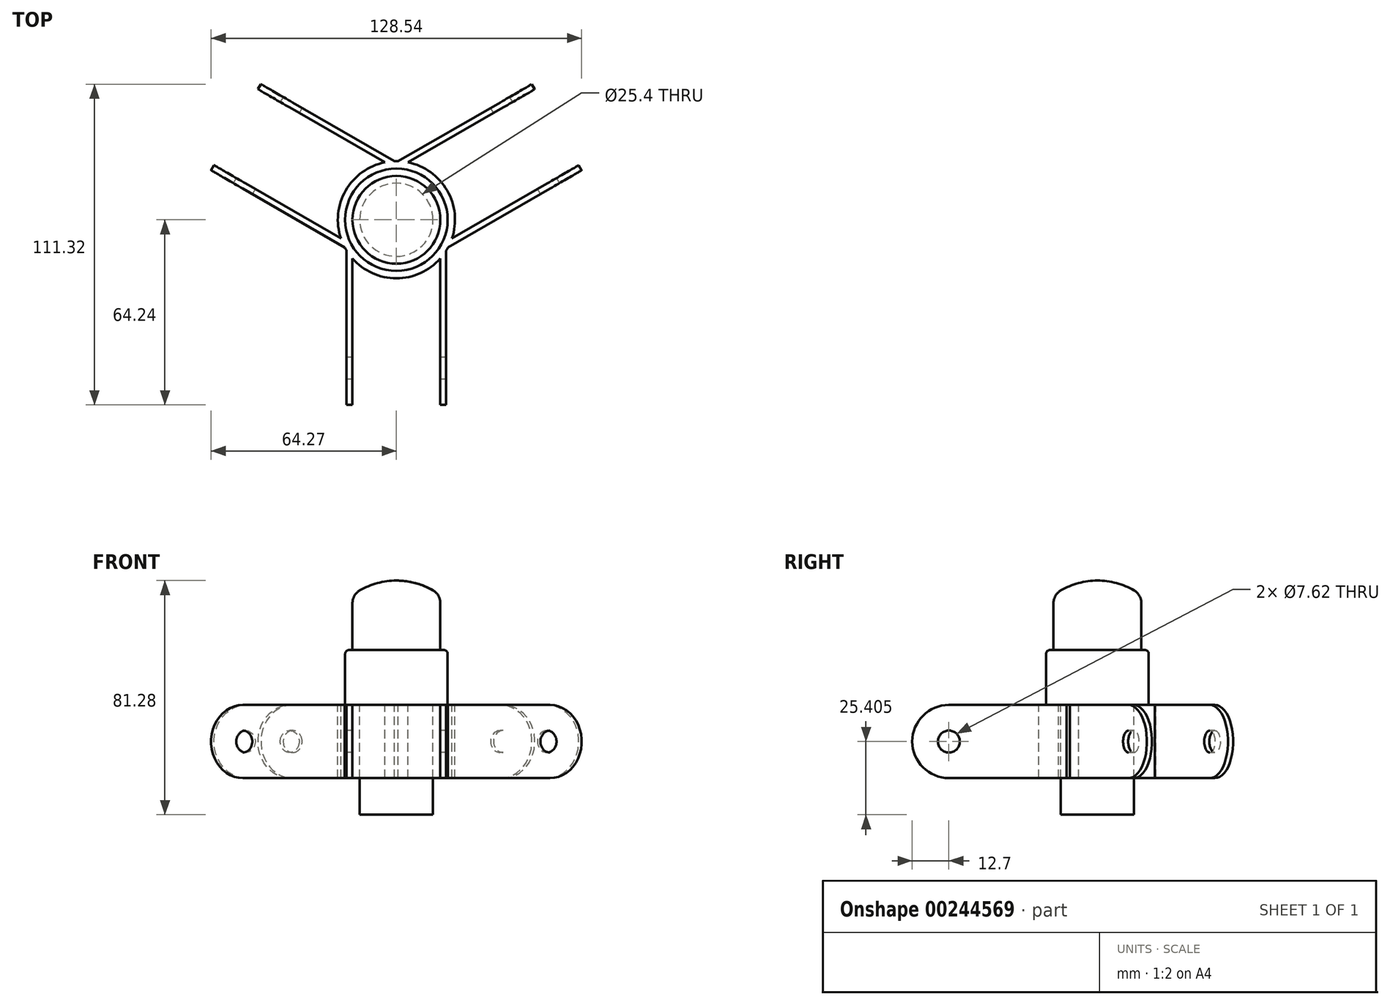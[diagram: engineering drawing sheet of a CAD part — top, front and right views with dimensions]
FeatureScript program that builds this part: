
annotation { "Feature Type Name" : "Feature", "Feature Type Description" : "" }
export const myFeature = defineFeature(function(context is Context, id is Id, definition is map)
    precondition{}
    {
        {
            var Q0;
            Q0=qCreatedBy(makeId("Front.planeOp"),FACE);
            var sketch = newSketch(context, id + "F0", { "sketchPlane" : qUnion([Q0])});
            skLineSegment(sketch, "E0.rect.top", {"start": v(15.24, -9.52) * mm, "end": v(0, -9.52) * mm});
            skLineSegment(sketch, "E0.rect.left", {"start": v(15.24, 9.53) * mm, "end": v(15.24, -9.52) * mm});
            skPoint(sketch, "E0.rect.middle", {"position": v(0, 0) * mm});
            skLineSegment(sketch, "E1", {"start": v(0, 65.3) * mm, "end": v(0, -40.02) * mm, "construction": true});
            skArc(sketch, "E2.0.MirrorCS", {"start": v(0, 14.6) * mm, "mid": v(8.03, 13.3) * mm, "end": v(15.24, 9.53) * mm});
            skLineSegment(sketch, "E3", {"start": v(0, 14.6) * mm, "end": v(0, -9.52) * mm});
            skPoint(sketch, "E4.center.orphan", {"position": v(0, -12.6) * mm});
            skPoint(sketch, "E0.rect.right.start.orphan", {"position": v(-15.24, 9.53) * mm});
            skPoint(sketch, "E5.orphan", {"position": v(-15.24, -9.52) * mm});
            skSolve(sketch);
        }
        {
            var Q0;
            Q0=makeQuery(id+"F0.imprint","IMPRINT",FACE,{"disambiguationData":[TD([[makeQuery(id+"F0.imprint","IMPRINT",EDGE,{"derivedFrom":sQuery(id+"F0.wireOp",EDGE,"E0.rect.top")}),-1.0]])]});
            var Q1;
            Q1=sQuery(id+"F0.wireOp",EDGE,"E1");
            revolve(context, id + "F1", {"entities" : qUnion([Q0]), "axis" : qUnion([Q1]), "revolveType" : RevolveType.FULL});
        }
        {
            var Q0;
            Q0=makeQuery(id+"F1.opRevolve","SWEPT_EDGE",EDGE,{"disambiguationData":[OSD([sQuery(id+"F0.wireOp",EDGE,"E0.rect.left"),sQuery(id+"F0.wireOp",EDGE,"E2.0.MirrorCS")])]});
            fillet(context, id + "F2", {"entities" : qUnion([Q0]), "radius" : 5.08 * mm, "tangentPropagation" : true, "allowEdgeOverflow" : false});
        }
        {
            var Q0;
            Q0=makeQuery(id+"F1.opRevolve","SWEPT_FACE",FACE,{"disambiguationData":[OSD([sQuery(id+"F0.wireOp",EDGE,"E0.rect.top")])]});
            var sketch = newSketch(context, id + "F3", { "sketchPlane" : qUnion([Q0])});
            skCircle(sketch, "E6", {"center": v(0, 0) * mm, "radius": 17.78 * mm});
            skSolve(sketch);
        }
        {
            var Q0;
            Q0=makeQuery(id+"F3.imprint","IMPRINT",FACE,{"disambiguationData":[TD([[makeQuery(id+"F3.imprint","IMPRINT",EDGE,{"derivedFrom":sQuery(id+"F3.wireOp",EDGE,"E6")}),1.0]])]});
            var Q1;
            Q1=makeQuery(id+"F3.imprint","IMPRINT",FACE,{"disambiguationData":[TD([[makeQuery(id+"F3.imprint","IMPRINT",EDGE,{"derivedFrom":makeQuery(id+"F1.opRevolve","SWEPT_EDGE",EDGE,{"disambiguationData":[OSD([sQuery(id+"F0.wireOp",EDGE,"E0.rect.top"),sQuery(id+"F0.wireOp",EDGE,"E0.rect.left")])]})}),-1.0]])]});
            extrude(context, id + "F4", {"entities" : qUnion([Q0, Q1]), "operationType" : NewBodyOperationType.ADD, "depth" : 19.05 * mm});
        }
        {
            var Q0;
            Q0=makeQuery(id+"F4.opExtrude","CAP_FACE",FACE,{"disambiguationData":[OSD([sQuery(id+"F3.wireOp",EDGE,"E6")])],"isStart":false});
            var sketch = newSketch(context, id + "F5", { "sketchPlane" : qUnion([Q0])});
            skCircle(sketch, "E7.0", {"center": v(0, 0) * mm, "radius": 12.7 * mm});
            skCircle(sketch, "E8.0", {"center": v(0, 0) * mm, "radius": 15.24 * mm});
            skSolve(sketch);
        }
        {
            var Q0;
            Q0=makeQuery(id+"F5.imprint","IMPRINT",FACE,{"disambiguationData":[TD([[makeQuery(id+"F5.imprint","IMPRINT",EDGE,{"derivedFrom":sQuery(id+"F5.wireOp",EDGE,"E7.0")}),1.0]])]});
            extrude(context, id + "F6", {"entities" : qUnion([Q0]), "operationType" : NewBodyOperationType.ADD, "depth" : 38.1 * mm});
        }
        {
            var Q0;
            {var subQ0=sQuery(id+"F3.wireOp",EDGE,"E6");Q0=makeQuery(id+"F6.boolean.opBoolean","SPLIT",FACE,{"disambiguationData":[TD([makeQuery(id+"F4.opExtrude","SWEPT_FACE",FACE,{"disambiguationData":[OSD([subQ0])]})])],"derivedFrom":makeQuery(id+"F4.opExtrude","CAP_FACE",FACE,{"disambiguationData":[OSD([subQ0])],"isStart":false})});}
            var sketch = newSketch(context, id + "F7", { "sketchPlane" : qUnion([Q0])});
            skArc(sketch, "E9", {"start": v(15.24, 13.44) * mm, "mid": v(0, 20.32) * mm, "end": v(-15.24, 13.44) * mm});
            skLineSegment(sketch, "E10", {"start": v(-15.24, 13.44) * mm, "end": v(-15.24, 64.24) * mm});
            skLineSegment(sketch, "E11", {"start": v(15.24, 13.44) * mm, "end": v(15.24, 64.24) * mm});
            skLineSegment(sketch, "E12", {"start": v(15.24, 64.24) * mm, "end": v(-15.24, 64.24) * mm, "construction": true});
            skLineSegment(sketch, "E13", {"start": v(-17.27, 64.24) * mm, "end": v(-17.27, 10.7) * mm});
            skLineSegment(sketch, "E14", {"start": v(-17.27, 10.7) * mm, "end": v(17.27, 10.7) * mm, "construction": true});
            skLineSegment(sketch, "E15", {"start": v(17.27, 10.7) * mm, "end": v(17.27, 64.24) * mm});
            skLineSegment(sketch, "E16", {"start": v(17.27, 64.24) * mm, "end": v(15.24, 64.24) * mm});
            skLineSegment(sketch, "E17", {"start": v(-17.27, 64.24) * mm, "end": v(-15.24, 64.24) * mm});
            skArc(sketch, "E18.trimOffspring", {"start": v(-17.27, 10.7) * mm, "mid": v(-17.6, 10.16) * mm, "end": v(-17.9, 9.6) * mm});
            skLineSegment(sketch, "E19.1.0", {"start": v(-19.26, 6.48) * mm, "end": v(-63.25, -18.92) * mm});
            skLineSegment(sketch, "E19.1.1", {"start": v(-4.02, -19.92) * mm, "end": v(-48.01, -45.32) * mm});
            skLineSegment(sketch, "E19.1.2", {"start": v(-47, -47.08) * mm, "end": v(-0.63, -20.31) * mm});
            skLineSegment(sketch, "E19.1.3", {"start": v(-64.27, -17.16) * mm, "end": v(-63.25, -18.92) * mm});
            skLineSegment(sketch, "E19.1.4", {"start": v(-17.9, 9.6) * mm, "end": v(-64.27, -17.16) * mm});
            skLineSegment(sketch, "E19.1.5", {"start": v(-47, -47.08) * mm, "end": v(-48.01, -45.32) * mm});
            skLineSegment(sketch, "E19.2.0", {"start": v(4.02, -19.92) * mm, "end": v(48.01, -45.32) * mm});
            skLineSegment(sketch, "E19.2.1", {"start": v(19.26, 6.48) * mm, "end": v(63.25, -18.92) * mm});
            skLineSegment(sketch, "E19.2.2", {"start": v(64.27, -17.16) * mm, "end": v(17.9, 9.6) * mm});
            skLineSegment(sketch, "E19.2.3", {"start": v(47, -47.08) * mm, "end": v(48.01, -45.32) * mm});
            skLineSegment(sketch, "E19.2.4", {"start": v(0.63, -20.31) * mm, "end": v(47, -47.08) * mm});
            skLineSegment(sketch, "E19.2.5", {"start": v(64.27, -17.16) * mm, "end": v(63.25, -18.92) * mm});
            skArc(sketch, "E20.trimOffspring", {"start": v(17.9, 9.6) * mm, "mid": v(17.6, 10.16) * mm, "end": v(17.27, 10.7) * mm});
            skArc(sketch, "E21.trimOffspring", {"start": v(4.02, -19.92) * mm, "mid": v(17.6, -10.16) * mm, "end": v(19.26, 6.48) * mm});
            skArc(sketch, "E22.trimOffspring", {"start": v(-0.63, -20.31) * mm, "mid": v(0, -20.32) * mm, "end": v(0.63, -20.31) * mm});
            skArc(sketch, "E23.trimOffspring", {"start": v(-19.26, 6.48) * mm, "mid": v(-17.6, -10.16) * mm, "end": v(-4.02, -19.92) * mm});
            skSolve(sketch);
        }
        {
            var Q0;
            Q0=makeQuery(id+"F7.imprint","IMPRINT",FACE,{"disambiguationData":[TD([[makeQuery(id+"F7.imprint","IMPRINT",EDGE,{"derivedFrom":sQuery(id+"F7.wireOp",EDGE,"E9")}),1.0]])]});
            var Q1;
            Q1=makeQuery(id+"F7.imprint","IMPRINT",FACE,{"disambiguationData":[TD([[makeQuery(id+"F7.imprint","IMPRINT",EDGE,{"derivedFrom":makeQuery(id+"F4.opExtrude","CAP_EDGE",EDGE,{"disambiguationData":[OSD([sQuery(id+"F3.wireOp",EDGE,"E6")])],"isStart":false})}),1.0]])]});
            extrude(context, id + "F8", {"entities" : qUnion([Q0, Q1]), "depth" : 25.4 * mm});
        }
        {
            var Q0;
            Q0=qCreatedBy(makeId("Right.planeOp"),FACE);
            var sketch = newSketch(context, id + "F9", { "sketchPlane" : qUnion([Q0])});
            skArc(sketch, "E24", {"start": v(-51.54, -28.57) * mm, "mid": v(-64.24, -41.27) * mm, "end": v(-51.54, -53.98) * mm});
            skLineSegment(sketch, "E25", {"start": v(-51.54, -28.58) * mm, "end": v(-65.97, -14.17) * mm});
            skLineSegment(sketch, "E26", {"start": v(-65.97, -14.17) * mm, "end": v(-83.5, -41.67) * mm});
            skLineSegment(sketch, "E27", {"start": v(-83.5, -41.67) * mm, "end": v(-61.4, -63.09) * mm});
            skLineSegment(sketch, "E28", {"start": v(-61.4, -63.09) * mm, "end": v(-51.54, -53.98) * mm});
            skCircle(sketch, "E29", {"center": v(-51.54, -41.27) * mm, "radius": 3.81 * mm});
            skSolve(sketch);
        }
        {
            var Q0;
            Q0=makeQuery(id+"F9.imprint","IMPRINT",FACE,{"disambiguationData":[TD([[makeQuery(id+"F9.imprint","IMPRINT",EDGE,{"derivedFrom":sQuery(id+"F9.wireOp",EDGE,"E24")}),-1.0]])]});
            var Q1;
            Q1=makeQuery(id+"F9.imprint","IMPRINT",FACE,{"disambiguationData":[TD([[makeQuery(id+"F9.imprint","IMPRINT",EDGE,{"derivedFrom":sQuery(id+"F9.wireOp",EDGE,"E29")}),1.0]])]});
            extrude(context, id + "F10", {"entities" : qUnion([Q0, Q1]), "operationType" : NewBodyOperationType.REMOVE, "endBound" : BoundingType.SYMMETRIC, "oppositeDirection" : true, "depth" : 76.2 * mm});
        }
        {
            var Q0;
            Q0=makeQuery(id+"F8.opExtrude","SWEPT_BODY",BODY,{"disambiguationData":[OSD([sQuery(id+"F5.wireOp",EDGE,"E8.0"),sQuery(id+"F7.wireOp",EDGE,"E9"),sQuery(id+"F7.wireOp",EDGE,"E10"),sQuery(id+"F7.wireOp",EDGE,"E11"),sQuery(id+"F7.wireOp",EDGE,"E13"),sQuery(id+"F7.wireOp",EDGE,"E15"),sQuery(id+"F7.wireOp",EDGE,"E16"),sQuery(id+"F7.wireOp",EDGE,"E17"),sQuery(id+"F7.wireOp",EDGE,"E18.trimOffspring"),sQuery(id+"F7.wireOp",EDGE,"E19.1.0"),sQuery(id+"F7.wireOp",EDGE,"E19.1.1"),sQuery(id+"F7.wireOp",EDGE,"E19.1.2"),sQuery(id+"F7.wireOp",EDGE,"E19.1.3"),sQuery(id+"F7.wireOp",EDGE,"E19.1.4"),sQuery(id+"F7.wireOp",EDGE,"E19.1.5"),sQuery(id+"F7.wireOp",EDGE,"E19.2.0"),sQuery(id+"F7.wireOp",EDGE,"E19.2.1"),sQuery(id+"F7.wireOp",EDGE,"E19.2.2"),sQuery(id+"F7.wireOp",EDGE,"E19.2.3"),sQuery(id+"F7.wireOp",EDGE,"E19.2.4"),sQuery(id+"F7.wireOp",EDGE,"E19.2.5"),sQuery(id+"F7.wireOp",EDGE,"E20.trimOffspring"),sQuery(id+"F7.wireOp",EDGE,"E21.trimOffspring"),sQuery(id+"F7.wireOp",EDGE,"E22.trimOffspring"),sQuery(id+"F7.wireOp",EDGE,"E23.trimOffspring")])]});
            var Q1;
            Q1=makeQuery(id+"F4.opExtrude","SWEPT_FACE",FACE,{"disambiguationData":[OSD([sQuery(id+"F3.wireOp",EDGE,"E6")])]});
            circularPattern(context, id + "F11", {"entities" : qUnion([Q0]), "axis" : qUnion([Q1]), "angle" : 120 * degree, "instanceCount" : 3});
        }
        {
            var Q0;
            Q0=makeQuery(id+"F8.opExtrude","SWEPT_FACE",FACE,{"disambiguationData":[OSD([sQuery(id+"F7.wireOp",EDGE,"E13")])]});
            var sketch = newSketch(context, id + "F12", { "sketchPlane" : qUnion([Q0])});
            skCircle(sketch, "E30.0", {"center": v(51.54, -41.27) * mm, "radius": 3.81 * mm});
            skArc(sketch, "E31.0", {"start": v(51.54, -28.57) * mm, "mid": v(64.24, -41.27) * mm, "end": v(51.54, -53.98) * mm});
            skLineSegment(sketch, "E32", {"start": v(51.54, -28.57) * mm, "end": v(69, -20.65) * mm});
            skLineSegment(sketch, "E33", {"start": v(69, -20.65) * mm, "end": v(71.12, -31.87) * mm});
            skLineSegment(sketch, "E34", {"start": v(71.12, -31.87) * mm, "end": v(70.4, -53.4) * mm});
            skLineSegment(sketch, "E35", {"start": v(70.4, -53.4) * mm, "end": v(65.1, -63.01) * mm});
            skLineSegment(sketch, "E36", {"start": v(65.1, -63.01) * mm, "end": v(51.76, -54.24) * mm});
            skLineSegment(sketch, "E37", {"start": v(51.76, -54.24) * mm, "end": v(51.54, -53.98) * mm});
            skSolve(sketch);
        }
        {
            var Q0;
            Q0=makeQuery(id+"F12.imprint","IMPRINT",FACE,{"disambiguationData":[TD([[makeQuery(id+"F12.imprint","IMPRINT",EDGE,{"derivedFrom":sQuery(id+"F12.wireOp",EDGE,"E31.0")}),1.0]])]});
            var Q1;
            Q1=makeQuery(id+"F12.imprint","IMPRINT",FACE,{"disambiguationData":[TD([[makeQuery(id+"F12.imprint","IMPRINT",EDGE,{"derivedFrom":sQuery(id+"F12.wireOp",EDGE,"E30.0")}),-1.0]])]});
            extrude(context, id + "F13", {"entities" : qUnion([Q0, Q1]), "operationType" : NewBodyOperationType.REMOVE, "endBound" : BoundingType.SYMMETRIC, "oppositeDirection" : true, "depth" : 2667 * mm});
        }
        {
            var Q0;
            Q0=makeQuery(id+"F11.opPattern","COPY",FACE,{"derivedFrom":makeQuery(id+"F8.opExtrude","SWEPT_FACE",FACE,{"disambiguationData":[OSD([sQuery(id+"F7.wireOp",EDGE,"E15")])]}),"instanceName":"2"});
            var sketch = newSketch(context, id + "F14", { "sketchPlane" : qUnion([Q0])});
            skArc(sketch, "E38.0", {"start": v(-51.54, -53.98) * mm, "mid": v(-64.24, -41.28) * mm, "end": v(-51.54, -28.57) * mm});
            skCircle(sketch, "E39.0", {"center": v(-51.54, -41.27) * mm, "radius": 3.81 * mm});
            skLineSegment(sketch, "E40", {"start": v(-51.54, -28.57) * mm, "end": v(-74.34, -19.56) * mm});
            skLineSegment(sketch, "E41", {"start": v(-74.34, -19.56) * mm, "end": v(-71.54, -59.34) * mm});
            skLineSegment(sketch, "E42", {"start": v(-71.54, -59.34) * mm, "end": v(-60.38, -65.16) * mm});
            skLineSegment(sketch, "E43", {"start": v(-60.38, -65.16) * mm, "end": v(-51.54, -53.98) * mm});
            skSolve(sketch);
        }
        {
            var Q0;
            Q0=makeQuery(id+"F14.imprint","IMPRINT",FACE,{"disambiguationData":[TD([[makeQuery(id+"F14.imprint","IMPRINT",EDGE,{"derivedFrom":sQuery(id+"F14.wireOp",EDGE,"E38.0")}),1.0]])]});
            var Q1;
            Q1=makeQuery(id+"F14.imprint","IMPRINT",FACE,{"disambiguationData":[TD([[makeQuery(id+"F14.imprint","IMPRINT",EDGE,{"derivedFrom":sQuery(id+"F14.wireOp",EDGE,"E39.0")}),-1.0]])]});
            extrude(context, id + "F15", {"entities" : qUnion([Q0, Q1]), "operationType" : NewBodyOperationType.REMOVE, "oppositeDirection" : true, "depth" : 38.1 * mm});
        }
        {
            var Q0;
            Q0=makeQuery(id+"F11.opPattern","COPY",FACE,{"derivedFrom":makeQuery(id+"F8.opExtrude","SWEPT_FACE",FACE,{"disambiguationData":[OSD([sQuery(id+"F7.wireOp",EDGE,"E15")])]}),"instanceName":"1"});
            var sketch = newSketch(context, id + "F16", { "sketchPlane" : qUnion([Q0])});
            skArc(sketch, "E44.0", {"start": v(-51.54, -53.98) * mm, "mid": v(-64.24, -41.28) * mm, "end": v(-51.54, -28.57) * mm});
            skCircle(sketch, "E45.0", {"center": v(-51.54, -41.27) * mm, "radius": 3.81 * mm});
            skLineSegment(sketch, "E46", {"start": v(-51.54, -28.57) * mm, "end": v(-67.35, -14.85) * mm});
            skLineSegment(sketch, "E47", {"start": v(-67.35, -14.85) * mm, "end": v(-81.57, -40.09) * mm});
            skLineSegment(sketch, "E48", {"start": v(-81.57, -40.09) * mm, "end": v(-76.74, -62.05) * mm});
            skLineSegment(sketch, "E49", {"start": v(-76.74, -62.05) * mm, "end": v(-61.74, -66.29) * mm});
            skLineSegment(sketch, "E50", {"start": v(-61.74, -66.29) * mm, "end": v(-51.54, -53.98) * mm});
            skSolve(sketch);
        }
        {
            var Q0;
            Q0=makeQuery(id+"F16.imprint","IMPRINT",FACE,{"disambiguationData":[TD([[makeQuery(id+"F16.imprint","IMPRINT",EDGE,{"derivedFrom":sQuery(id+"F16.wireOp",EDGE,"E44.0")}),1.0]])]});
            var Q1;
            Q1=makeQuery(id+"F16.imprint","IMPRINT",FACE,{"disambiguationData":[TD([[makeQuery(id+"F16.imprint","IMPRINT",EDGE,{"derivedFrom":sQuery(id+"F16.wireOp",EDGE,"E45.0")}),-1.0]])]});
            extrude(context, id + "F17", {"entities" : qUnion([Q0, Q1]), "operationType" : NewBodyOperationType.REMOVE, "oppositeDirection" : true, "depth" : 38.1 * mm});
        }
        {
            var Q0;
            Q0=makeQuery(id+"F11.opPattern","COPY",BODY,{"derivedFrom":makeQuery(id+"F8.opExtrude","SWEPT_BODY",BODY,{"disambiguationData":[OSD([sQuery(id+"F5.wireOp",EDGE,"E8.0"),sQuery(id+"F7.wireOp",EDGE,"E9"),sQuery(id+"F7.wireOp",EDGE,"E10"),sQuery(id+"F7.wireOp",EDGE,"E11"),sQuery(id+"F7.wireOp",EDGE,"E13"),sQuery(id+"F7.wireOp",EDGE,"E15"),sQuery(id+"F7.wireOp",EDGE,"E16"),sQuery(id+"F7.wireOp",EDGE,"E17"),sQuery(id+"F7.wireOp",EDGE,"E18.trimOffspring"),sQuery(id+"F7.wireOp",EDGE,"E19.1.0"),sQuery(id+"F7.wireOp",EDGE,"E19.1.1"),sQuery(id+"F7.wireOp",EDGE,"E19.1.2"),sQuery(id+"F7.wireOp",EDGE,"E19.1.3"),sQuery(id+"F7.wireOp",EDGE,"E19.1.4"),sQuery(id+"F7.wireOp",EDGE,"E19.1.5"),sQuery(id+"F7.wireOp",EDGE,"E19.2.0"),sQuery(id+"F7.wireOp",EDGE,"E19.2.1"),sQuery(id+"F7.wireOp",EDGE,"E19.2.2"),sQuery(id+"F7.wireOp",EDGE,"E19.2.3"),sQuery(id+"F7.wireOp",EDGE,"E19.2.4"),sQuery(id+"F7.wireOp",EDGE,"E19.2.5"),sQuery(id+"F7.wireOp",EDGE,"E20.trimOffspring"),sQuery(id+"F7.wireOp",EDGE,"E21.trimOffspring"),sQuery(id+"F7.wireOp",EDGE,"E22.trimOffspring"),sQuery(id+"F7.wireOp",EDGE,"E23.trimOffspring")])]}),"instanceName":"2"});
            deleteBodies(context, id + "F18", {"entities" : qUnion([Q0])});
        }
        {
            var Q0;
            Q0=makeQuery(id+"F8.opExtrude","SWEPT_BODY",BODY,{"disambiguationData":[OSD([sQuery(id+"F5.wireOp",EDGE,"E8.0"),sQuery(id+"F7.wireOp",EDGE,"E9"),sQuery(id+"F7.wireOp",EDGE,"E10"),sQuery(id+"F7.wireOp",EDGE,"E11"),sQuery(id+"F7.wireOp",EDGE,"E13"),sQuery(id+"F7.wireOp",EDGE,"E15"),sQuery(id+"F7.wireOp",EDGE,"E16"),sQuery(id+"F7.wireOp",EDGE,"E17"),sQuery(id+"F7.wireOp",EDGE,"E18.trimOffspring"),sQuery(id+"F7.wireOp",EDGE,"E19.1.0"),sQuery(id+"F7.wireOp",EDGE,"E19.1.1"),sQuery(id+"F7.wireOp",EDGE,"E19.1.2"),sQuery(id+"F7.wireOp",EDGE,"E19.1.3"),sQuery(id+"F7.wireOp",EDGE,"E19.1.4"),sQuery(id+"F7.wireOp",EDGE,"E19.1.5"),sQuery(id+"F7.wireOp",EDGE,"E19.2.0"),sQuery(id+"F7.wireOp",EDGE,"E19.2.1"),sQuery(id+"F7.wireOp",EDGE,"E19.2.2"),sQuery(id+"F7.wireOp",EDGE,"E19.2.3"),sQuery(id+"F7.wireOp",EDGE,"E19.2.4"),sQuery(id+"F7.wireOp",EDGE,"E19.2.5"),sQuery(id+"F7.wireOp",EDGE,"E20.trimOffspring"),sQuery(id+"F7.wireOp",EDGE,"E21.trimOffspring"),sQuery(id+"F7.wireOp",EDGE,"E22.trimOffspring"),sQuery(id+"F7.wireOp",EDGE,"E23.trimOffspring")])]});
            deleteBodies(context, id + "F19", {"entities" : qUnion([Q0])});
        }
        {
            var Q0;
            Q0=makeQuery(id+"F1.opRevolve","SWEPT_EDGE",EDGE,{"disambiguationData":[OSD([sQuery(id+"F0.wireOp",EDGE,"E0.rect.top"),sQuery(id+"F0.wireOp",EDGE,"E0.rect.left")])]});
            var Q1;
            Q1=makeQuery(id+"F4.opExtrude","CAP_EDGE",EDGE,{"disambiguationData":[OSD([sQuery(id+"F3.wireOp",EDGE,"E6")])],"isStart":true});
            fillet(context, id + "F20", {"entities" : qUnion([Q0, Q1]), "radius" : 1.27 * mm, "tangentPropagation" : true, "allowEdgeOverflow" : false});
        }
    });
